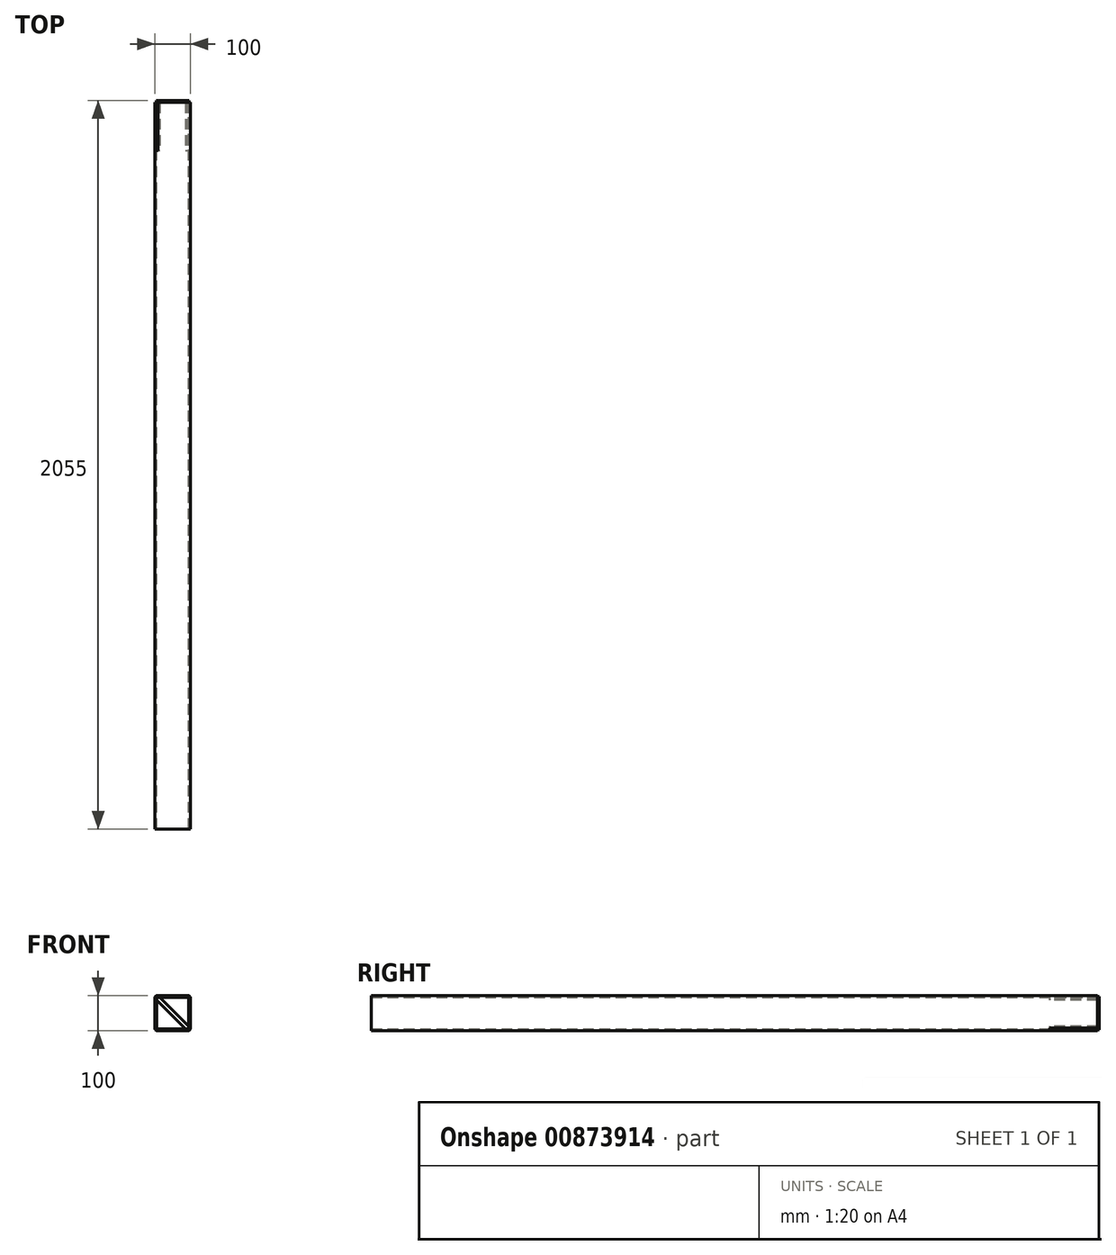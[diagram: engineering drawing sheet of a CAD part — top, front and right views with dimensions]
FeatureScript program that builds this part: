
annotation { "Feature Type Name" : "Feature", "Feature Type Description" : "" }
export const myFeature = defineFeature(function(context is Context, id is Id, definition is map)
    precondition{}
    {
        {
            var Q0;
            Q0=qCreatedBy(makeId("Front.planeOp"),FACE);
            var sketch = newSketch(context, id + "F0", { "sketchPlane" : qUnion([Q0])});
            skLineSegment(sketch, "E0.bottom", {"start": v(43, 50) * mm, "end": v(-43, 50) * mm});
            skLineSegment(sketch, "E0.top", {"start": v(43, -50) * mm, "end": v(-43, -50) * mm});
            skLineSegment(sketch, "E0.left", {"start": v(50, 43) * mm, "end": v(50, -43) * mm});
            skLineSegment(sketch, "E0.right", {"start": v(-50, 43) * mm, "end": v(-50, -43) * mm});
            skPoint(sketch, "E0.middle", {"position": v(0, 0) * mm});
            skPoint(sketch, "E1.visualSharp", {"position": v(-50, 50) * mm});
            skArc(sketch, "E1.filletArc", {"start": v(-43, 50) * mm, "mid": v(-47.95, 47.95) * mm, "end": v(-50, 43) * mm});
            skPoint(sketch, "E2.visualSharp", {"position": v(50, 50) * mm});
            skArc(sketch, "E2.filletArc", {"start": v(50, 43) * mm, "mid": v(47.95, 47.95) * mm, "end": v(43, 50) * mm});
            skPoint(sketch, "E3.visualSharp", {"position": v(-50, -50) * mm});
            skArc(sketch, "E3.filletArc", {"start": v(-50, -43) * mm, "mid": v(-47.95, -47.95) * mm, "end": v(-43, -50) * mm});
            skPoint(sketch, "E4.visualSharp", {"position": v(50, -50) * mm});
            skArc(sketch, "E4.filletArc", {"start": v(43, -50) * mm, "mid": v(47.95, -47.95) * mm, "end": v(50, -43) * mm});
            skLineSegment(sketch, "E5.0", {"start": v(43, -45) * mm, "end": v(-43, -45) * mm});
            skArc(sketch, "E5.1", {"start": v(-45, -43) * mm, "mid": v(-44.41, -44.41) * mm, "end": v(-43, -45) * mm});
            skArc(sketch, "E5.2", {"start": v(43, -45) * mm, "mid": v(44.41, -44.41) * mm, "end": v(45, -43) * mm});
            skLineSegment(sketch, "E5.3", {"start": v(-45, 43) * mm, "end": v(-45, -43) * mm});
            skLineSegment(sketch, "E5.4", {"start": v(45, 43) * mm, "end": v(45, -43) * mm});
            skArc(sketch, "E5.5", {"start": v(45, 43) * mm, "mid": v(44.41, 44.41) * mm, "end": v(43, 45) * mm});
            skLineSegment(sketch, "E5.6", {"start": v(43, 45) * mm, "end": v(-43, 45) * mm});
            skArc(sketch, "E5.7", {"start": v(-43, 45) * mm, "mid": v(-44.41, 44.41) * mm, "end": v(-45, 43) * mm});
            skSolve(sketch);
        }
        {
            var Q0;
            Q0=makeQuery(id+"F0.imprint","IMPRINT",FACE,{"disambiguationData":[TD([[makeQuery(id+"F0.imprint","IMPRINT",EDGE,{"derivedFrom":sQuery(id+"F0.wireOp",EDGE,"E0.bottom")}),1.0]])]});
            extrude(context, id + "F1", {"entities" : qUnion([Q0]), "depth" : 2050 * mm, "offsetDistance" : 25 * mm, "symmetric" : true});
        }
        {
            var Q0;
            Q0=makeQuery(id+"F1.opExtrude","CAP_FACE",FACE,{"disambiguationData":[OSD([sQuery(id+"F0.wireOp",EDGE,"E0.bottom"),sQuery(id+"F0.wireOp",EDGE,"E0.top"),sQuery(id+"F0.wireOp",EDGE,"E0.left"),sQuery(id+"F0.wireOp",EDGE,"E0.right"),sQuery(id+"F0.wireOp",EDGE,"E1.filletArc"),sQuery(id+"F0.wireOp",EDGE,"E2.filletArc"),sQuery(id+"F0.wireOp",EDGE,"E3.filletArc"),sQuery(id+"F0.wireOp",EDGE,"E4.filletArc"),sQuery(id+"F0.wireOp",EDGE,"E5.0"),sQuery(id+"F0.wireOp",EDGE,"E5.1"),sQuery(id+"F0.wireOp",EDGE,"E5.2"),sQuery(id+"F0.wireOp",EDGE,"E5.3"),sQuery(id+"F0.wireOp",EDGE,"E5.4"),sQuery(id+"F0.wireOp",EDGE,"E5.5"),sQuery(id+"F0.wireOp",EDGE,"E5.6"),sQuery(id+"F0.wireOp",EDGE,"E5.7")])],"isStart":true});
            var sketch = newSketch(context, id + "F2", { "sketchPlane" : qUnion([Q0])});
            skLineSegment(sketch, "E6.bottom", {"start": v(46.5, 46.5) * mm, "end": v(-46.5, 46.5) * mm});
            skLineSegment(sketch, "E6.top", {"start": v(46.5, -46.5) * mm, "end": v(-46.5, -46.5) * mm});
            skLineSegment(sketch, "E6.left", {"start": v(46.5, 46.5) * mm, "end": v(46.5, -46.5) * mm});
            skLineSegment(sketch, "E6.right", {"start": v(-46.5, 46.5) * mm, "end": v(-46.5, -46.5) * mm});
            skPoint(sketch, "E6.middle", {"position": v(0, 0) * mm});
            skSolve(sketch);
        }
        {
            var Q0;
            Q0 = qSketchRegion(id + "F2", true);
            extrude(context, id + "F3", {"entities" : qUnion([Q0]), "depth" : 5 * mm, "offsetDistance" : 25 * mm});
        }
        {
            var Q0;
            Q0=makeQuery(id+"F1.opExtrude","CAP_FACE",FACE,{"disambiguationData":[OSD([sQuery(id+"F0.wireOp",EDGE,"E0.bottom"),sQuery(id+"F0.wireOp",EDGE,"E0.top"),sQuery(id+"F0.wireOp",EDGE,"E0.left"),sQuery(id+"F0.wireOp",EDGE,"E0.right"),sQuery(id+"F0.wireOp",EDGE,"E1.filletArc"),sQuery(id+"F0.wireOp",EDGE,"E2.filletArc"),sQuery(id+"F0.wireOp",EDGE,"E3.filletArc"),sQuery(id+"F0.wireOp",EDGE,"E4.filletArc"),sQuery(id+"F0.wireOp",EDGE,"E5.0"),sQuery(id+"F0.wireOp",EDGE,"E5.1"),sQuery(id+"F0.wireOp",EDGE,"E5.2"),sQuery(id+"F0.wireOp",EDGE,"E5.3"),sQuery(id+"F0.wireOp",EDGE,"E5.4"),sQuery(id+"F0.wireOp",EDGE,"E5.5"),sQuery(id+"F0.wireOp",EDGE,"E5.6"),sQuery(id+"F0.wireOp",EDGE,"E5.7")])],"isStart":true});
            var sketch = newSketch(context, id + "F4", { "sketchPlane" : qUnion([Q0])});
            skLineSegment(sketch, "E7.bottom", {"start": v(57.28, 48.8) * mm, "end": v(48.8, 57.28) * mm});
            skLineSegment(sketch, "E7.top", {"start": v(-48.8, -57.28) * mm, "end": v(-57.28, -48.8) * mm});
            skLineSegment(sketch, "E7.left", {"start": v(57.28, 48.8) * mm, "end": v(-48.8, -57.28) * mm});
            skLineSegment(sketch, "E7.right", {"start": v(48.8, 57.28) * mm, "end": v(-57.28, -48.8) * mm});
            skPoint(sketch, "E7.middle", {"position": v(0, 0) * mm});
            skSolve(sketch);
        }
        {
            var Q0;
            Q0 = qSketchRegion(id + "F4", true);
            extrude(context, id + "F5", {"entities" : qUnion([Q0]), "operationType" : NewBodyOperationType.REMOVE, "oppositeDirection" : true, "depth" : 270 * mm, "offsetDistance" : 25 * mm, "symmetric" : true});
        }
    });
